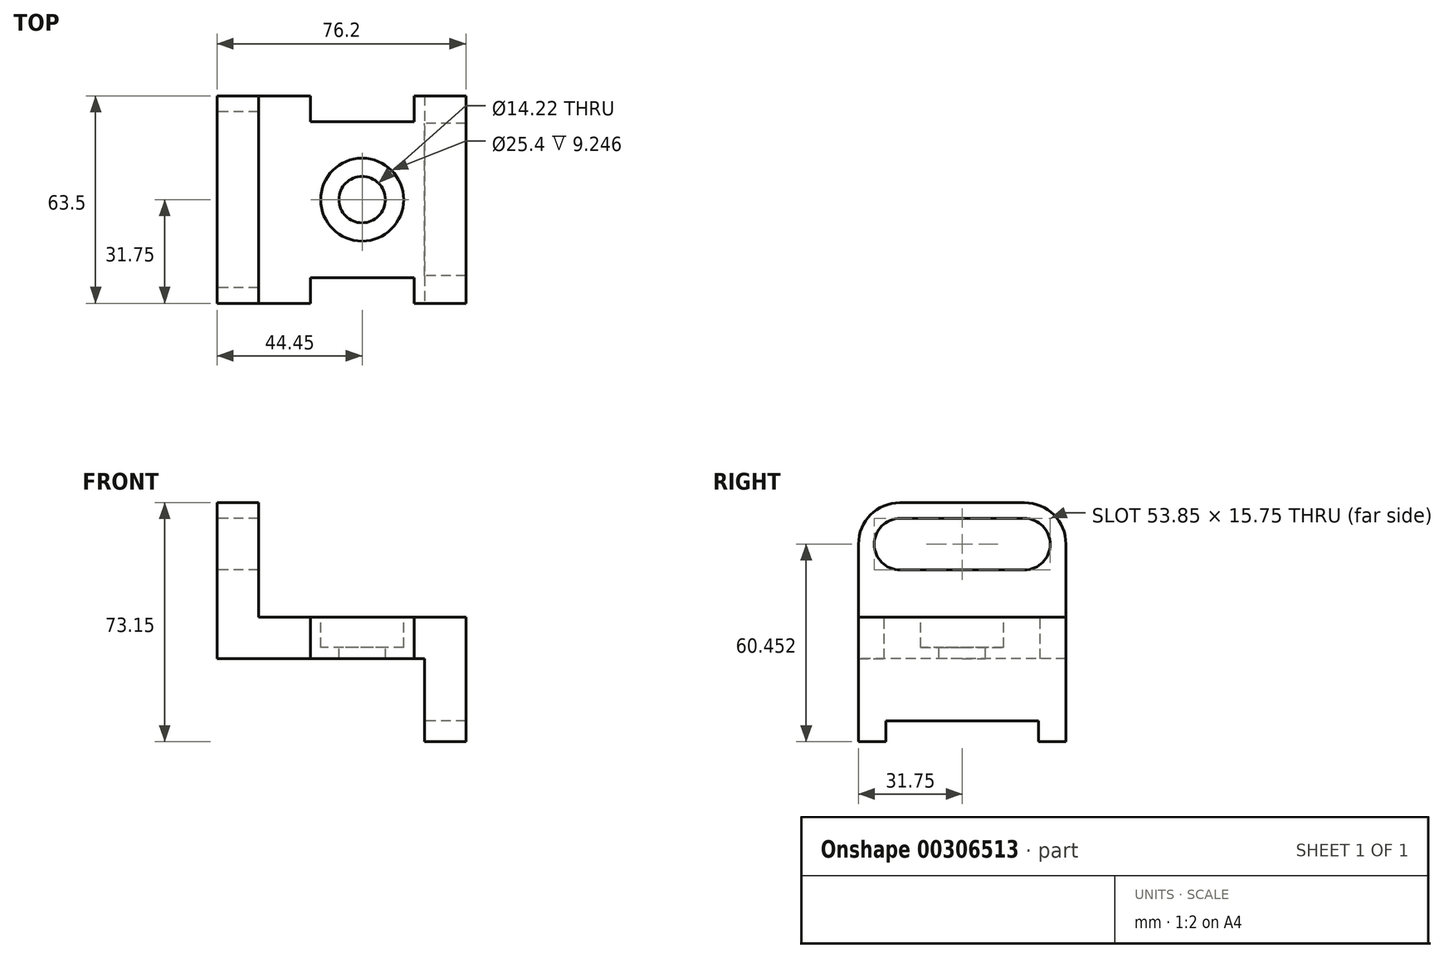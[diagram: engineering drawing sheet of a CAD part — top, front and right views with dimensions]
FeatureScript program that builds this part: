
annotation { "Feature Type Name" : "Feature", "Feature Type Description" : "" }
export const myFeature = defineFeature(function(context is Context, id is Id, definition is map)
    precondition{}
    {
        {
            var Q0;
            Q0=qCreatedBy(makeId("Right.planeOp"),FACE);
            var sketch = newSketch(context, id + "F0", { "sketchPlane" : qUnion([Q0])});
            skLineSegment(sketch, "E0", {"start": v(0, 0) * mm, "end": v(8.42, 0) * mm});
            skLineSegment(sketch, "E1", {"start": v(8.42, 0) * mm, "end": v(8.42, 6.35) * mm});
            skLineSegment(sketch, "E2", {"start": v(8.42, 6.35) * mm, "end": v(55.08, 6.35) * mm});
            skLineSegment(sketch, "E3", {"start": v(55.08, 6.35) * mm, "end": v(55.08, 0) * mm});
            skLineSegment(sketch, "E4", {"start": v(55.08, 0) * mm, "end": v(63.5, 0) * mm});
            skLineSegment(sketch, "E5", {"start": v(63.5, 0) * mm, "end": v(63.5, 38.1) * mm});
            skLineSegment(sketch, "E6", {"start": v(63.5, 38.1) * mm, "end": v(0, 38.1) * mm});
            skLineSegment(sketch, "E7", {"start": v(0, 38.1) * mm, "end": v(0, 0) * mm});
            skLineSegment(sketch, "E8", {"start": v(0, 38.1) * mm, "end": v(0, 60.45) * mm});
            skLineSegment(sketch, "E9", {"start": v(12.7, 73.15) * mm, "end": v(50.8, 73.15) * mm});
            skLineSegment(sketch, "E10", {"start": v(63.5, 38.1) * mm, "end": v(63.5, 60.45) * mm});
            skArc(sketch, "E11", {"start": v(50.8, 73.15) * mm, "mid": v(59.78, 69.43) * mm, "end": v(63.5, 60.45) * mm});
            skArc(sketch, "E12", {"start": v(12.7, 68.33) * mm, "mid": v(4.83, 60.45) * mm, "end": v(12.7, 52.58) * mm});
            skArc(sketch, "E13", {"start": v(50.8, 68.33) * mm, "mid": v(58.67, 60.45) * mm, "end": v(50.8, 52.58) * mm});
            skLineSegment(sketch, "E14", {"start": v(12.7, 68.33) * mm, "end": v(50.8, 68.33) * mm});
            skLineSegment(sketch, "E15", {"start": v(50.8, 52.58) * mm, "end": v(12.7, 52.58) * mm});
            skArc(sketch, "E16", {"start": v(0, 60.45) * mm, "mid": v(3.72, 69.43) * mm, "end": v(12.7, 73.15) * mm});
            skSolve(sketch);
        }
        {
            var Q0;
            Q0=makeQuery(id+"F0.imprint","IMPRINT",FACE,{"disambiguationData":[TD([[makeQuery(id+"F0.imprint","IMPRINT",EDGE,{"derivedFrom":sQuery(id+"F0.wireOp",EDGE,"E6")}),-1.0]])]});
            extrude(context, id + "F1", {"entities" : qUnion([Q0]), "depth" : 12.7 * mm});
        }
        {
            var Q0;
            Q0=makeQuery(id+"F0.imprint","IMPRINT",FACE,{"disambiguationData":[TD([[makeQuery(id+"F0.imprint","IMPRINT",EDGE,{"derivedFrom":sQuery(id+"F0.wireOp",EDGE,"E0")}),1.0]])]});
            extrude(context, id + "F2", {"entities" : qUnion([Q0]), "operationType" : NewBodyOperationType.ADD, "depth" : 76.2 * mm});
        }
        {
            var Q0;
            Q0=makeQuery(id+"F2.opExtrude","SWEPT_FACE",FACE,{"disambiguationData":[OSD([sQuery(id+"F0.wireOp",EDGE,"E6")])]});
            var sketch = newSketch(context, id + "F3", { "sketchPlane" : qUnion([Q0])});
            skCircle(sketch, "E17", {"center": v(44.45, 31.75) * mm, "radius": 12.7 * mm});
            skCircle(sketch, "E18", {"center": v(44.45, 31.75) * mm, "radius": 7.11 * mm});
            skLineSegment(sketch, "E19", {"start": v(12.7, 63.5) * mm, "end": v(12.7, 0) * mm});
            skLineSegment(sketch, "E20", {"start": v(12.7, 0) * mm, "end": v(28.58, 0) * mm});
            skLineSegment(sketch, "E21", {"start": v(28.58, 0) * mm, "end": v(28.58, 7.87) * mm});
            skLineSegment(sketch, "E22", {"start": v(28.58, 7.87) * mm, "end": v(60.33, 7.87) * mm});
            skLineSegment(sketch, "E23", {"start": v(60.33, 7.87) * mm, "end": v(60.33, 0) * mm});
            skLineSegment(sketch, "E24", {"start": v(60.33, 0) * mm, "end": v(76.2, 0) * mm});
            skLineSegment(sketch, "E25", {"start": v(76.2, 0) * mm, "end": v(76.2, 63.5) * mm});
            skLineSegment(sketch, "E26", {"start": v(76.2, 63.5) * mm, "end": v(60.33, 63.5) * mm});
            skLineSegment(sketch, "E27", {"start": v(60.33, 63.5) * mm, "end": v(60.33, 55.63) * mm});
            skLineSegment(sketch, "E28", {"start": v(60.33, 55.63) * mm, "end": v(28.58, 55.63) * mm});
            skLineSegment(sketch, "E29", {"start": v(28.58, 55.63) * mm, "end": v(28.58, 63.5) * mm});
            skLineSegment(sketch, "E30", {"start": v(28.58, 63.5) * mm, "end": v(12.7, 63.5) * mm});
            skLineSegment(sketch, "E31", {"start": v(28.58, 63.5) * mm, "end": v(60.33, 63.5) * mm});
            skLineSegment(sketch, "E32", {"start": v(28.58, 0) * mm, "end": v(60.33, 0) * mm});
            skSolve(sketch);
        }
        {
            var Q0;
            Q0=makeQuery(id+"F3.imprint","IMPRINT",FACE,{"disambiguationData":[TD([[makeQuery(id+"F3.imprint","IMPRINT",EDGE,{"derivedFrom":sQuery(id+"F3.wireOp",EDGE,"E17")}),1.0]])]});
            extrude(context, id + "F4", {"entities" : qUnion([Q0]), "operationType" : NewBodyOperationType.REMOVE, "oppositeDirection" : true, "depth" : 9.25 * mm});
        }
        {
            var Q0;
            Q0=makeQuery(id+"F3.imprint","IMPRINT",FACE,{"disambiguationData":[TD([[makeQuery(id+"F3.imprint","IMPRINT",EDGE,{"derivedFrom":sQuery(id+"F3.wireOp",EDGE,"E18")}),1.0]])]});
            extrude(context, id + "F5", {"entities" : qUnion([Q0]), "operationType" : NewBodyOperationType.REMOVE, "endBound" : BoundingType.THROUGH_ALL, "oppositeDirection" : true, "depth" : 25.4 * mm});
        }
        {
            var Q0;
            Q0=makeQuery(id+"F3.imprint","IMPRINT",FACE,{"disambiguationData":[TD([[makeQuery(id+"F3.imprint","IMPRINT",EDGE,{"derivedFrom":sQuery(id+"F3.wireOp",EDGE,"E27")}),-1.0]])]});
            var Q1;
            Q1=makeQuery(id+"F3.imprint","IMPRINT",FACE,{"disambiguationData":[TD([[makeQuery(id+"F3.imprint","IMPRINT",EDGE,{"derivedFrom":sQuery(id+"F3.wireOp",EDGE,"E21")}),-1.0]])]});
            extrude(context, id + "F6", {"entities" : qUnion([Q0, Q1]), "operationType" : NewBodyOperationType.REMOVE, "endBound" : BoundingType.THROUGH_ALL, "oppositeDirection" : true, "depth" : 25.4 * mm});
        }
        {
            var Q0;
            {var subQ0=sQuery(id+"F0.wireOp",EDGE,"E16");var subQ8=sQuery(id+"F0.wireOp",EDGE,"E8");var subQ11=sQuery(id+"F0.wireOp",EDGE,"E7");Q0=makeQuery(id+"F6.boolean.opBoolean","SPLIT",FACE,{"disambiguationData":[TD([makeQuery(id+"F1.opExtrude","SWEPT_FACE",FACE,{"disambiguationData":[OSD([subQ0])]})])],"derivedFrom":makeQuery(id+"F2.boolean.opBoolean","MERGE",FACE,{"derivedFrom":[makeQuery(id+"F1.opExtrude","SWEPT_FACE",FACE,{"disambiguationData":[OSD([subQ8])]}),makeQuery(id+"F2.opExtrude","SWEPT_FACE",FACE,{"disambiguationData":[OSD([subQ11])]})]})});}
            var sketch = newSketch(context, id + "F7", { "sketchPlane" : qUnion([Q0])});
            skLineSegment(sketch, "E33.bottom", {"start": v(0, 0) * mm, "end": v(63.5, 0) * mm});
            skLineSegment(sketch, "E33.top", {"start": v(0, 25.4) * mm, "end": v(63.5, 25.4) * mm});
            skLineSegment(sketch, "E33.left", {"start": v(0, 0) * mm, "end": v(0, 25.4) * mm});
            skLineSegment(sketch, "E33.right", {"start": v(63.5, 0) * mm, "end": v(63.5, 25.4) * mm});
            skSolve(sketch);
        }
        {
            var Q0;
            Q0 = qSketchRegion(id + "F7", true);
            extrude(context, id + "F8", {"entities" : qUnion([Q0]), "operationType" : NewBodyOperationType.REMOVE, "endBound" : BoundingType.THROUGH_ALL, "oppositeDirection" : true, "depth" : 25.4 * mm});
        }
    });
